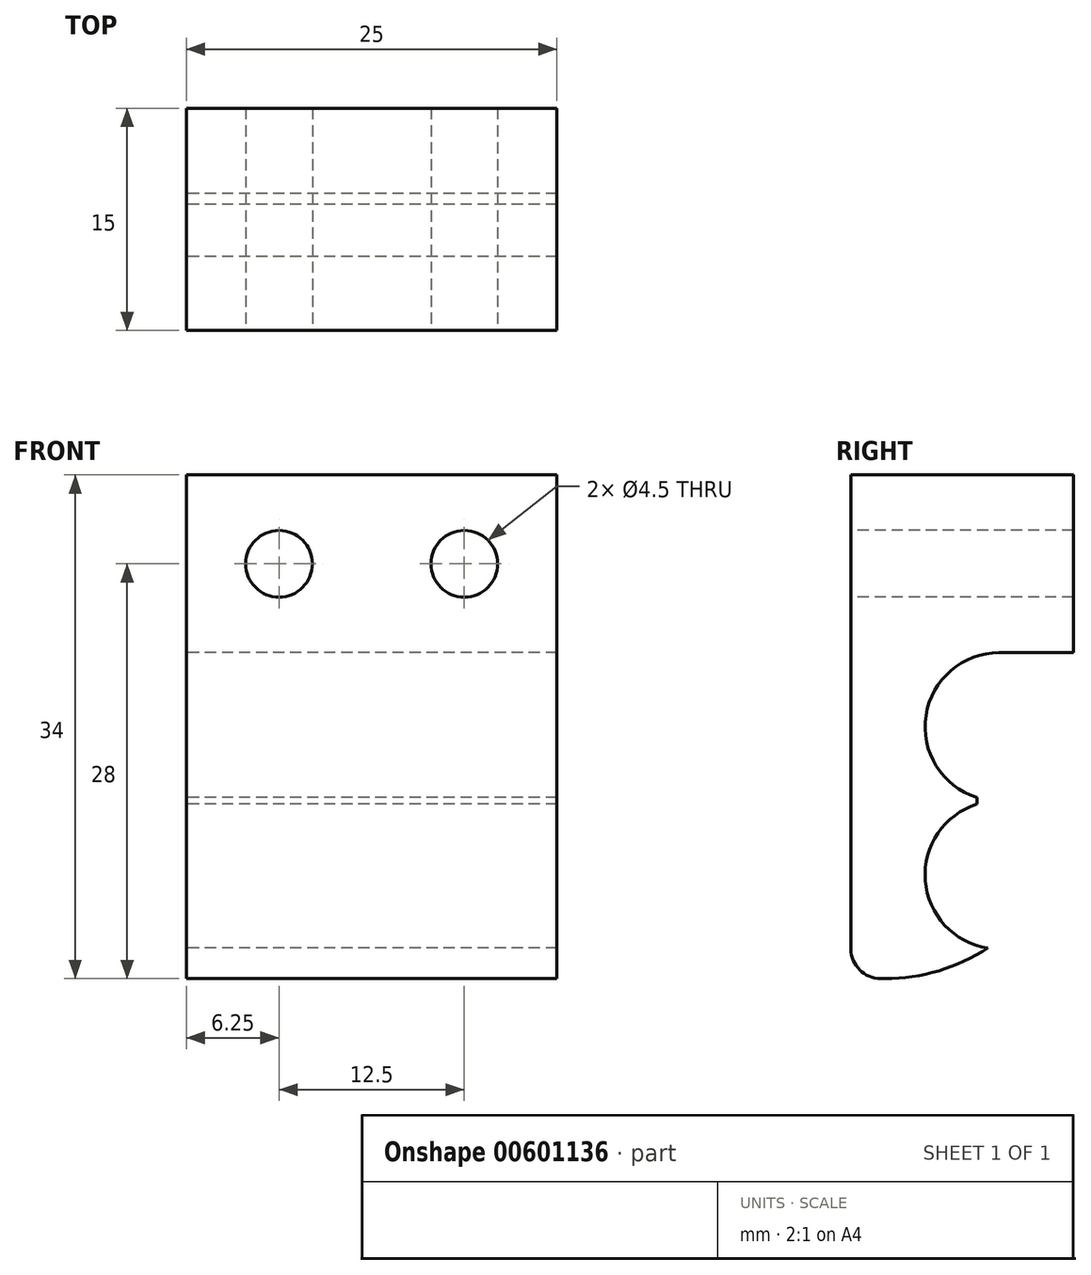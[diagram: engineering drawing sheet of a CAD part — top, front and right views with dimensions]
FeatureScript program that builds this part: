
annotation { "Feature Type Name" : "Feature", "Feature Type Description" : "" }
export const myFeature = defineFeature(function(context is Context, id is Id, definition is map)
    precondition{}
    {
        {
            var Q0;
            Q0=qCreatedBy(makeId("Right.planeOp"),FACE);
            var sketch = newSketch(context, id + "F0", { "sketchPlane" : qUnion([Q0])});
            skLineSegment(sketch, "E0", {"start": v(2, 0) * mm, "end": v(2.3, 0) * mm});
            skLineSegment(sketch, "E1", {"start": v(15, 22) * mm, "end": v(15, 34) * mm});
            skLineSegment(sketch, "E2", {"start": v(15, 34) * mm, "end": v(0, 34) * mm});
            skLineSegment(sketch, "E3", {"start": v(0, 34) * mm, "end": v(0, 2) * mm});
            skPoint(sketch, "E4.visualSharp", {"position": v(15, 0) * mm});
            skArc(sketch, "E4.filletArc", {"start": v(2.3, 0) * mm, "mid": v(5.92, 0.53) * mm, "end": v(9.23, 2.06) * mm});
            skArc(sketch, "E5", {"start": v(8.5, 11.77) * mm, "mid": v(5.01, 6.62) * mm, "end": v(9.23, 2.06) * mm});
            skArc(sketch, "E6", {"start": v(10, 22) * mm, "mid": v(5.06, 17.76) * mm, "end": v(8.5, 12.23) * mm});
            skPoint(sketch, "E7.visualSharp", {"position": v(0, 0) * mm});
            skArc(sketch, "E7.filletArc", {"start": v(0, 2) * mm, "mid": v(0.59, 0.59) * mm, "end": v(2, 0) * mm});
            skLineSegment(sketch, "E8", {"start": v(10, 22) * mm, "end": v(15, 22) * mm});
            skLineSegment(sketch, "E9", {"start": v(8.5, 12.23) * mm, "end": v(8.5, 11.77) * mm});
            skSolve(sketch);
        }
        {
            var Q0;
            Q0=makeQuery(id+"F0.imprint","IMPRINT",FACE,{"disambiguationData":[TD([[makeQuery(id+"F0.imprint","IMPRINT",EDGE,{"derivedFrom":sQuery(id+"F0.wireOp",EDGE,"E0")}),1.0]])]});
            extrude(context, id + "F1", {"entities" : qUnion([Q0]), "depth" : 25 * mm, "offsetDistance" : 25 * mm});
        }
        {
            var Q0;
            Q0=makeQuery(id+"F1.opExtrude","SWEPT_FACE",FACE,{"disambiguationData":[OSD([sQuery(id+"F0.wireOp",EDGE,"E3")])]});
            var sketch = newSketch(context, id + "F2", { "sketchPlane" : qUnion([Q0])});
            skCircle(sketch, "E10", {"center": v(6.25, 28) * mm, "radius": 2.25 * mm});
            skCircle(sketch, "E11", {"center": v(18.75, 28) * mm, "radius": 2.25 * mm});
            skSolve(sketch);
        }
        {
            var Q0;
            Q0 = qSketchRegion(id + "F2", true);
            extrude(context, id + "F3", {"entities" : qUnion([Q0]), "operationType" : NewBodyOperationType.REMOVE, "oppositeDirection" : true, "depth" : 28.7 * mm, "offsetDistance" : 25 * mm});
        }
        {
            var Q0;
            Q0=makeQuery(id+"F1.opExtrude","SWEPT_FACE",FACE,{"disambiguationData":[OSD([sQuery(id+"F0.wireOp",EDGE,"E3")])]});
            var sketch = newSketch(context, id + "F4", { "sketchPlane" : qUnion([Q0])});
            skCircle(sketch, "E12", {"center": v(6.25, 28) * mm, "radius": 4.25 * mm});
            skCircle(sketch, "E13", {"center": v(18.75, 28) * mm, "radius": 4.25 * mm});
            skSolve(sketch);
        }
        {
            var Q0;
            Q0=makeQuery(id+"F4.imprint","IMPRINT",FACE,{"disambiguationData":[TD([[makeQuery(id+"F4.imprint","IMPRINT",EDGE,{"derivedFrom":sQuery(id+"F4.wireOp",EDGE,"E12")}),1.0]])]});
            var Q1;
            Q1=makeQuery(id+"F4.imprint","IMPRINT",FACE,{"disambiguationData":[TD([[makeQuery(id+"F4.imprint","IMPRINT",EDGE,{"derivedFrom":sQuery(id+"F4.wireOp",EDGE,"E12")}),-1.0]])]});
            extrude(context, id + "F5", {"entities" : qUnion([Q0, Q1]), "operationType" : NewBodyOperationType.ADD, "depth" : -2 * mm, "offsetDistance" : 25 * mm});
        }
    });
